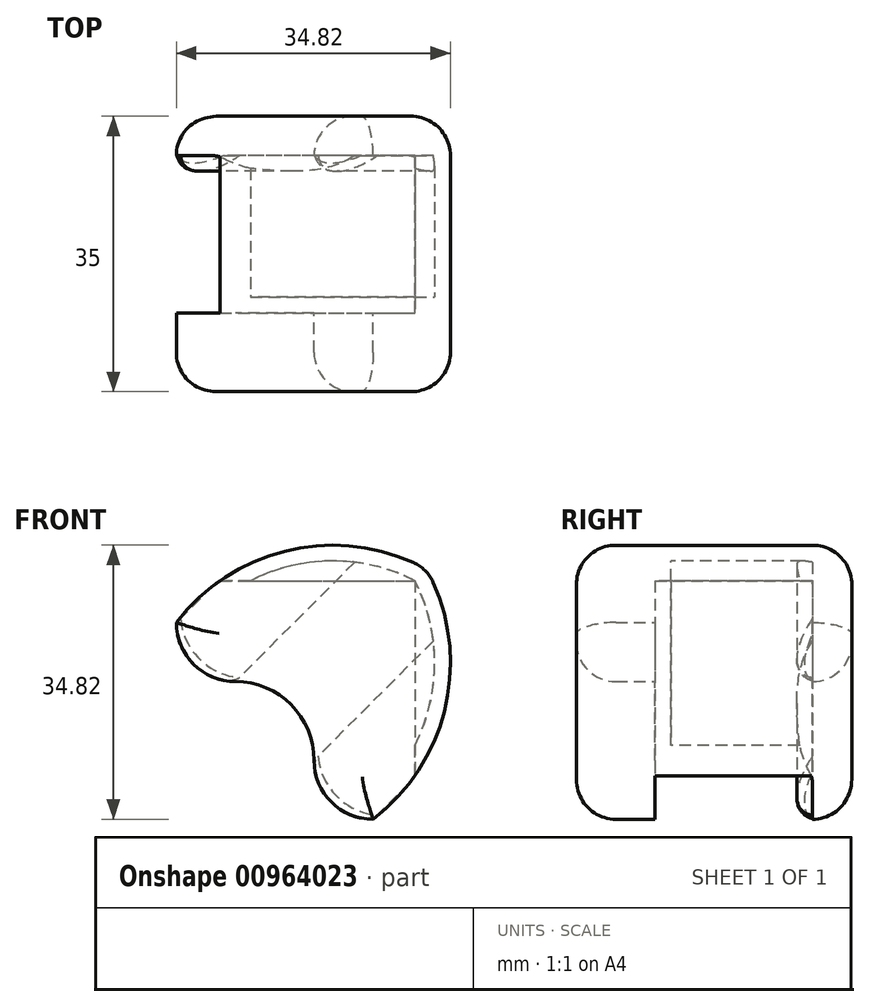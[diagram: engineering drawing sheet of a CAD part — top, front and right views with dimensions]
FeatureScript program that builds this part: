
annotation { "Feature Type Name" : "Feature", "Feature Type Description" : "" }
export const myFeature = defineFeature(function(context is Context, id is Id, definition is map)
    precondition{}
    {
        {
            var Q0;
            Q0=qCreatedBy(makeId("Front.planeOp"),FACE);
            var sketch = newSketch(context, id + "F0", { "sketchPlane" : qUnion([Q0])});
            skArc(sketch, "E0", {"start": v(10, 0) * mm, "mid": v(9.24, 3.83) * mm, "end": v(7.07, 7.07) * mm});
            skArc(sketch, "E1", {"start": v(10, 0) * mm, "mid": v(12.2, -5.3) * mm, "end": v(17.5, -7.5) * mm});
            skLineSegment(sketch, "E2", {"start": v(17.5, -38.8) * mm, "end": v(17.5, 17.5) * mm, "construction": true});
            skLineSegment(sketch, "E3", {"start": v(0, 0) * mm, "end": v(17.5, 17.5) * mm, "construction": true});
            skArc(sketch, "E4.MirrorCS", {"start": v(0, 10) * mm, "mid": v(3.83, 9.24) * mm, "end": v(7.07, 7.07) * mm});
            skLineSegment(sketch, "E5.MirrorCS", {"start": v(-38.8, 17.5) * mm, "end": v(17.5, 17.5) * mm, "construction": true});
            skArc(sketch, "E6.MirrorCS", {"start": v(0, 10) * mm, "mid": v(-5.3, 12.2) * mm, "end": v(-7.5, 17.5) * mm});
            skLineSegment(sketch, "E7", {"start": v(0, 6.4) * mm, "end": v(0, -12.33) * mm, "construction": true});
            skLineSegment(sketch, "E8", {"start": v(17.5, 17.5) * mm, "end": v(29.4, 29.4) * mm, "construction": true});
            skArc(sketch, "E9", {"start": v(17.5, -7.5) * mm, "mid": v(26.77, 7.14) * mm, "end": v(24.29, 24.29) * mm});
            skArc(sketch, "E10.MirrorCS", {"start": v(-7.5, 17.5) * mm, "mid": v(7.14, 26.77) * mm, "end": v(24.29, 24.29) * mm});
            skSolve(sketch);
        }
        {
            var Q0;
            Q0 = qSketchRegion(id + "F0", true);
            extrude(context, id + "F1", {"entities" : qUnion([Q0]), "depth" : 35 * mm, "offsetDistance" : 25 * mm});
        }
        {
            var Q0;
            Q0=makeQuery(id+"F1.opExtrude","CAP_EDGE",EDGE,{"disambiguationData":[OSD([sQuery(id+"F0.wireOp",EDGE,"E10.MirrorCS")])],"isStart":false});
            var Q1;
            Q1=makeQuery(id+"F1.opExtrude","CAP_EDGE",EDGE,{"disambiguationData":[OSD([sQuery(id+"F0.wireOp",EDGE,"E9")])],"isStart":false});
            var Q2;
            Q2=makeQuery(id+"F1.opExtrude","CAP_EDGE",EDGE,{"disambiguationData":[OSD([sQuery(id+"F0.wireOp",EDGE,"E0"),sQuery(id+"F0.wireOp",EDGE,"E4.MirrorCS")])],"isStart":false});
            var Q3;
            Q3=makeQuery(id+"F1.opExtrude","CAP_EDGE",EDGE,{"disambiguationData":[OSD([sQuery(id+"F0.wireOp",EDGE,"E10.MirrorCS")])],"isStart":true});
            var Q4;
            Q4=makeQuery(id+"F1.opExtrude","CAP_EDGE",EDGE,{"disambiguationData":[OSD([sQuery(id+"F0.wireOp",EDGE,"E9")])],"isStart":true});
            var Q5;
            Q5=makeQuery(id+"F1.opExtrude","CAP_EDGE",EDGE,{"disambiguationData":[OSD([sQuery(id+"F0.wireOp",EDGE,"E0"),sQuery(id+"F0.wireOp",EDGE,"E4.MirrorCS")])],"isStart":true});
            var Q6;
            Q6=makeQuery(id+"F1.opExtrude","SWEPT_EDGE",EDGE,{"disambiguationData":[OSD([sQuery(id+"F0.wireOp",EDGE,"E9"),sQuery(id+"F0.wireOp",EDGE,"E10.MirrorCS")])]});
            fillet(context, id + "F2", {"entities" : qUnion([Q0, Q1, Q2, Q3, Q4, Q5, Q6]), "radius" : 5 * mm, "tangentPropagation" : true, "allowEdgeOverflow" : false});
        }
        {
            var Q0;
            Q0=qCreatedBy(makeId("Front.planeOp"),FACE);
            var sketch = newSketch(context, id + "F3", { "sketchPlane" : qUnion([Q0])});
            skArc(sketch, "E11.0", {"start": v(0, 10) * mm, "mid": v(-5.3, 12.2) * mm, "end": v(-7.5, 17.5) * mm});
            skArc(sketch, "E11.1", {"start": v(10, 0) * mm, "mid": v(7.07, 7.07) * mm, "end": v(0, 10) * mm});
            skArc(sketch, "E11.2", {"start": v(17.5, -7.5) * mm, "mid": v(12.2, -5.3) * mm, "end": v(10, 0) * mm});
            skArc(sketch, "E11.3", {"start": v(-7.5, 17.5) * mm, "mid": v(6.23, 26.55) * mm, "end": v(22.61, 25.12) * mm});
            skArc(sketch, "E11.4", {"start": v(22.61, 25.12) * mm, "mid": v(24.1, 24.1) * mm, "end": v(25.12, 22.61) * mm});
            skArc(sketch, "E11.5", {"start": v(25.12, 22.61) * mm, "mid": v(26.55, 6.23) * mm, "end": v(17.5, -7.5) * mm});
            skArc(sketch, "E12.0", {"start": v(22.8, 22.8) * mm, "mid": v(24.82, 7.62) * mm, "end": v(16.85, -5.46) * mm});
            skArc(sketch, "E12.1", {"start": v(-5.46, 16.85) * mm, "mid": v(7.62, 24.82) * mm, "end": v(22.8, 22.8) * mm});
            skArc(sketch, "E12.2", {"start": v(16.85, -5.46) * mm, "mid": v(13.39, -3.65) * mm, "end": v(12, 0) * mm});
            skArc(sketch, "E12.3", {"start": v(12, 0) * mm, "mid": v(8.49, 8.49) * mm, "end": v(0, 12) * mm});
            skArc(sketch, "E12.4", {"start": v(0, 12) * mm, "mid": v(-3.65, 13.39) * mm, "end": v(-5.46, 16.85) * mm});
            skSolve(sketch);
        }
        {
            var Q0;
            Q0=sQuery(id+"F3.wireOp",EDGE,"E12.1");
            var Q1;
            Q1=sQuery(id+"F3.wireOp",EDGE,"E12.0");
            extrude(context, id + "F4", {"bodyType" : ToolBodyType.SURFACE, "surfaceEntities" : qUnion([Q0, Q1]), "depth" : 25 * mm, "offsetDistance" : 25 * mm});
        }
        {
            var Q0;
            {var subQ0=sQuery(id+"F0.wireOp",EDGE,"E6.MirrorCS");Q0=makeQuery(id+"F2.opFillet","BLEND_EDGE",EDGE,{"blendedFrom":[makeQuery(id+"F1.opExtrude","CAP_EDGE",EDGE,{"disambiguationData":[OSD([subQ0])],"isStart":false}),makeQuery(id+"F1.opExtrude","SWEPT_FACE",FACE,{"disambiguationData":[OSD([subQ0])]})],"blendedInto":[makeQuery(id+"F1.opExtrude","SWEPT_FACE",FACE,{"disambiguationData":[OSD([subQ0])]})]});}
            cPoint(context, id + "F5", {"entities" : qUnion([Q0]), "parameter" : 0.5});
        }
        {
            var Q0;
            {var subQ0=sQuery(id+"F0.wireOp",EDGE,"E1");Q0=makeQuery(id+"F2.opFillet","BLEND_EDGE",EDGE,{"blendedFrom":[makeQuery(id+"F1.opExtrude","CAP_EDGE",EDGE,{"disambiguationData":[OSD([subQ0])],"isStart":false}),makeQuery(id+"F1.opExtrude","SWEPT_FACE",FACE,{"disambiguationData":[OSD([subQ0])]})],"blendedInto":[makeQuery(id+"F1.opExtrude","SWEPT_FACE",FACE,{"disambiguationData":[OSD([subQ0])]})]});}
            cPoint(context, id + "F6", {"entities" : qUnion([Q0]), "parameter" : 0.5});
        }
        {
            var Q0;
            {var subQ0=sQuery(id+"F0.wireOp",EDGE,"E1");Q0=makeQuery(id+"F2.opFillet","BLEND_EDGE",EDGE,{"blendedFrom":[makeQuery(id+"F1.opExtrude","CAP_EDGE",EDGE,{"disambiguationData":[OSD([subQ0])],"isStart":true}),makeQuery(id+"F1.opExtrude","SWEPT_FACE",FACE,{"disambiguationData":[OSD([subQ0])]})],"blendedInto":[makeQuery(id+"F1.opExtrude","SWEPT_FACE",FACE,{"disambiguationData":[OSD([subQ0])]})]});}
            cPoint(context, id + "F7", {"entities" : qUnion([Q0]), "parameter" : 0.5});
        }
        {
            var Q0;
            Q0 = qCreatedBy(id + "F5" ,VERTEX);
            var Q1;
            Q1 = qCreatedBy(id + "F6" ,VERTEX);
            var Q2;
            Q2 = qCreatedBy(id + "F7" ,VERTEX);
            cPlane(context, id + "F8", {"entities" : qUnion([Q0, Q1, Q2]), "cplaneType" : CPlaneType.THREE_POINT, "offset" : 25 * mm, "width" : 150 * mm, "height" : 150 * mm});
        }
        {
            var Q0;
            Q0=qCreatedBy(id+"F8.planeOp",FACE);
            var sketch = newSketch(context, id + "F9", { "sketchPlane" : qUnion([Q0])});
            skLineSegment(sketch, "E13.0", {"start": v(23, 17.68) * mm, "end": v(5, 17.68) * mm});
            skLineSegment(sketch, "E13.1", {"start": v(23, -17.68) * mm, "end": v(5, -17.68) * mm});
            skLineSegment(sketch, "E13.2", {"start": v(23, -17.68) * mm, "end": v(23, -7.07) * mm});
            skLineSegment(sketch, "E13.3", {"start": v(23, -7.07) * mm, "end": v(23, 7.07) * mm});
            skLineSegment(sketch, "E13.4", {"start": v(23, 7.07) * mm, "end": v(23, 17.68) * mm});
            skLineSegment(sketch, "E13.6", {"start": v(5, 7.07) * mm, "end": v(5, -7.07) * mm});
            skArc(sketch, "E14", {"start": v(5, 7.07) * mm, "mid": v(7, 12.37) * mm, "end": v(5, 17.68) * mm});
            skArc(sketch, "E15", {"start": v(5, -17.68) * mm, "mid": v(7, -12.37) * mm, "end": v(5, -7.07) * mm});
            skPoint(sketch, "E16", {"position": v(5, -12.37) * mm});
            skLineSegment(sketch, "E17", {"start": v(-1.03, 12.37) * mm, "end": v(23, 12.37) * mm, "construction": true});
            skPoint(sketch, "E18", {"position": v(7, 12.37) * mm});
            skLineSegment(sketch, "E19", {"start": v(5, 17.68) * mm, "end": v(5, 7.07) * mm, "construction": true});
            skLineSegment(sketch, "E20", {"start": v(5, 0) * mm, "end": v(23, 0) * mm});
            skSolve(sketch);
        }
        {
            var Q0;
            Q0=makeQuery(id+"F9.imprint","IMPRINT",FACE,{"disambiguationData":[TD([[makeQuery(id+"F9.imprint","IMPRINT",EDGE,{"derivedFrom":sQuery(id+"F9.wireOp",EDGE,"E13.0")}),1.0]])]});
            var Q1;
            Q1=makeQuery(id+"F4.opExtrude","SWEPT_FACE",FACE,{"disambiguationData":[OSD([sQuery(id+"F3.wireOp",EDGE,"E12.1")])]});
            extrude(context, id + "F10", {"entities" : qUnion([Q0]), "operationType" : NewBodyOperationType.REMOVE, "endBound" : BoundingType.UP_TO_SURFACE, "oppositeDirection" : true, "depth" : 7.7 * mm, "endBoundEntityFace" : qUnion([Q1]), "offsetDistance" : 25 * mm});
        }
        {
            var Q0;
            Q0=makeQuery(id+"F9.imprint","IMPRINT",FACE,{"disambiguationData":[TD([[makeQuery(id+"F9.imprint","IMPRINT",EDGE,{"derivedFrom":sQuery(id+"F9.wireOp",EDGE,"E13.1")}),-1.0]])]});
            var Q1;
            Q1=makeQuery(id+"F4.opExtrude","SWEPT_FACE",FACE,{"disambiguationData":[OSD([sQuery(id+"F3.wireOp",EDGE,"E12.0")])]});
            extrude(context, id + "F11", {"entities" : qUnion([Q0]), "operationType" : NewBodyOperationType.REMOVE, "endBound" : BoundingType.UP_TO_SURFACE, "oppositeDirection" : true, "depth" : 25 * mm, "endBoundEntityFace" : qUnion([Q1]), "offsetDistance" : 25 * mm});
        }
        {
            var Q0;
            Q0=qCreatedBy(makeId("Front.planeOp"),FACE);
            var sketch = newSketch(context, id + "F12", { "sketchPlane" : qUnion([Q0])});
            skLineSegment(sketch, "E21", {"start": v(-24.71, 22.8) * mm, "end": v(22.8, 22.8) * mm});
            skLineSegment(sketch, "E22", {"start": v(22.8, 22.8) * mm, "end": v(22.8, -24.71) * mm});
            skLineSegment(sketch, "E23", {"start": v(-24.71, 22.8) * mm, "end": v(22.8, -24.71) * mm, "construction": true});
            skSolve(sketch);
        }
        {
            var Q0;
            Q0=sQuery(id+"F12.wireOp",EDGE,"E22");
            var Q1;
            Q1=sQuery(id+"F12.wireOp",EDGE,"E21");
            extrude(context, id + "F13", {"bodyType" : ToolBodyType.SURFACE, "surfaceEntities" : qUnion([Q0, Q1]), "depth" : 25 * mm, "offsetDistance" : 25 * mm});
        }
        {
            var Q0;
            Q0=qCreatedBy(id+"F8.planeOp",FACE);
            var sketch = newSketch(context, id + "F14", { "sketchPlane" : qUnion([Q0])});
            skLineSegment(sketch, "E24.0", {"start": v(25, 0) * mm, "end": v(25, 33.6) * mm});
            skLineSegment(sketch, "E24.3", {"start": v(25, -33.6) * mm, "end": v(25, 0) * mm});
            skLineSegment(sketch, "E24.4", {"start": v(5, -33.6) * mm, "end": v(25, -33.6) * mm});
            skLineSegment(sketch, "E24.5", {"start": v(25, 33.6) * mm, "end": v(5, 33.6) * mm});
            skArc(sketch, "E25.0", {"start": v(5, -17.68) * mm, "mid": v(7, -12.37) * mm, "end": v(5, -7.07) * mm});
            skArc(sketch, "E25.1", {"start": v(5, 7.07) * mm, "mid": v(7, 12.37) * mm, "end": v(5, 17.68) * mm});
            skLineSegment(sketch, "E25.2", {"start": v(5, 7.07) * mm, "end": v(5, -7.07) * mm});
            skLineSegment(sketch, "E26", {"start": v(5, 17.68) * mm, "end": v(5, 33.6) * mm});
            skLineSegment(sketch, "E27", {"start": v(5, -17.68) * mm, "end": v(5, -33.6) * mm});
            skLineSegment(sketch, "E28", {"start": v(25, 0) * mm, "end": v(5, 0) * mm});
            skSolve(sketch);
        }
        {
            var Q0;
            Q0=makeQuery(id+"F14.imprint","IMPRINT",FACE,{"disambiguationData":[TD([[makeQuery(id+"F14.imprint","IMPRINT",EDGE,{"derivedFrom":sQuery(id+"F14.wireOp",EDGE,"E24.0")}),1.0]])]});
            var Q1;
            Q1=makeQuery(id+"F13.opExtrude","SWEPT_FACE",FACE,{"disambiguationData":[OSD([sQuery(id+"F12.wireOp",EDGE,"E21")])]});
            extrude(context, id + "F15", {"entities" : qUnion([Q0]), "operationType" : NewBodyOperationType.REMOVE, "endBound" : BoundingType.UP_TO_SURFACE, "oppositeDirection" : true, "depth" : 25 * mm, "endBoundEntityFace" : qUnion([Q1]), "offsetDistance" : 25 * mm});
        }
        {
            var Q0;
            Q0=makeQuery(id+"F14.imprint","IMPRINT",FACE,{"disambiguationData":[TD([[makeQuery(id+"F14.imprint","IMPRINT",EDGE,{"derivedFrom":sQuery(id+"F14.wireOp",EDGE,"E24.3")}),1.0]])]});
            var Q1;
            Q1=makeQuery(id+"F13.opExtrude","SWEPT_FACE",FACE,{"disambiguationData":[OSD([sQuery(id+"F12.wireOp",EDGE,"E22")])]});
            extrude(context, id + "F16", {"entities" : qUnion([Q0]), "operationType" : NewBodyOperationType.REMOVE, "endBound" : BoundingType.UP_TO_SURFACE, "oppositeDirection" : true, "depth" : 25 * mm, "endBoundEntityFace" : qUnion([Q1]), "offsetDistance" : 25 * mm});
        }
        {
            var Q0;
            Q0=makeQuery(id+"F15.boolean.opBoolean","INTERSECT",EDGE,{"derivedFrom":[makeQuery(id+"F1.opExtrude","SWEPT_FACE",FACE,{"disambiguationData":[OSD([sQuery(id+"F0.wireOp",EDGE,"E6.MirrorCS")])]}),makeQuery(id+"F15.opExtrude","SWEPT_FACE",FACE,{"disambiguationData":[OSD([sQuery(id+"F14.wireOp",EDGE,"E25.1")])]})]});
            var Q1;
            Q1=makeQuery(id+"F16.boolean.opBoolean","INTERSECT",EDGE,{"derivedFrom":[makeQuery(id+"F1.opExtrude","SWEPT_FACE",FACE,{"disambiguationData":[OSD([sQuery(id+"F0.wireOp",EDGE,"E1")])]}),makeQuery(id+"F16.opExtrude","SWEPT_FACE",FACE,{"disambiguationData":[OSD([sQuery(id+"F14.wireOp",EDGE,"E25.0")])]})]});
            fillet(context, id + "F17", {"entities" : qUnion([Q0, Q1]), "radius" : 1 * mm, "tangentPropagation" : true, "allowEdgeOverflow" : false});
        }
    });
